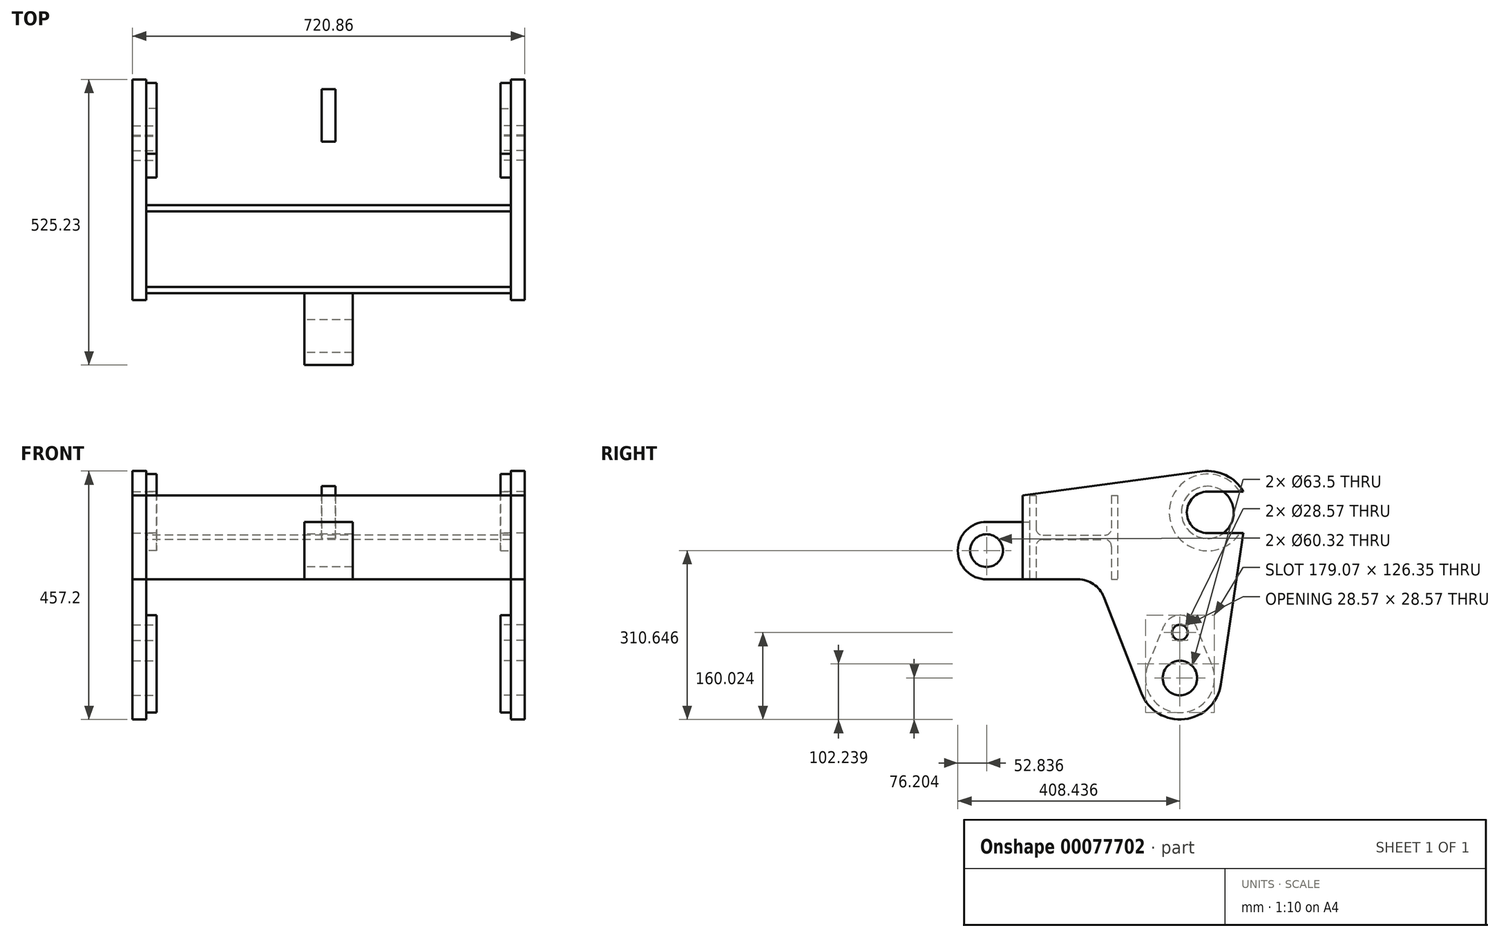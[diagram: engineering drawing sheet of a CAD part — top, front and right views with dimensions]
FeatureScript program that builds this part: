
annotation { "Feature Type Name" : "Feature", "Feature Type Description" : "" }
export const myFeature = defineFeature(function(context is Context, id is Id, definition is map)
    precondition{}
    {
        {
            var Q0;
            Q0=qCreatedBy(makeId("Right.planeOp"),FACE);
            var sketch = newSketch(context, id + "F0", { "sketchPlane" : qUnion([Q0])});
            skLineSegment(sketch, "E0.rect.bottom", {"start": v(-81.03, 77.22) * mm, "end": v(-69.47, 77.22) * mm});
            skLineSegment(sketch, "E0.rect.top", {"start": v(-81.03, -77.22) * mm, "end": v(-69.47, -77.22) * mm});
            skLineSegment(sketch, "E0.rect.left", {"start": v(-81.03, 77.22) * mm, "end": v(-81.03, -77.22) * mm});
            skLineSegment(sketch, "E0.rect.right", {"start": v(81.03, 77.22) * mm, "end": v(81.03, -77.22) * mm});
            skPoint(sketch, "E0.rect.middle", {"position": v(0, 0) * mm});
            skLineSegment(sketch, "E1.0", {"start": v(-69.47, 77.22) * mm, "end": v(-69.47, -77.22) * mm});
            skLineSegment(sketch, "E2", {"start": v(-81.03, 0) * mm, "end": v(81.03, 0) * mm, "construction": true});
            skLineSegment(sketch, "E3", {"start": v(0, 77.22) * mm, "end": v(0, -77.22) * mm, "construction": true});
            skLineSegment(sketch, "E4.0", {"start": v(-81.03, -4.06) * mm, "end": v(81.03, -4.06) * mm});
            skLineSegment(sketch, "E5.0.MirrorCS", {"start": v(-81.03, 4.06) * mm, "end": v(81.03, 4.06) * mm});
            skLineSegment(sketch, "E6.0.MirrorCS", {"start": v(69.47, 77.22) * mm, "end": v(69.47, -77.22) * mm});
            skLineSegment(sketch, "E7.trimOffspring", {"start": v(69.47, 77.22) * mm, "end": v(81.03, 77.22) * mm});
            skLineSegment(sketch, "E8.trimOffspring", {"start": v(69.47, -77.22) * mm, "end": v(81.03, -77.22) * mm});
            skSolve(sketch);
        }
        {
            var Q0;
            Q0=qSketchRegion(id+"F0",true);
            extrude(context, id + "F1", {"entities" : qUnion([Q0]), "endBound" : BoundingType.SYMMETRIC, "depth" : 670.05 * mm});
        }
        {
            var Q0;
            Q0=makeQuery(id+"F1.opExtrude","SWEPT_EDGE",EDGE,{"disambiguationData":[OSD([sQuery(id+"F0.wireOp",EDGE,"E5.0.MirrorCS"),sQuery(id+"F0.wireOp",EDGE,"E6.0.MirrorCS")])]});
            var Q1;
            Q1=makeQuery(id+"F1.opExtrude","SWEPT_EDGE",EDGE,{"disambiguationData":[OSD([sQuery(id+"F0.wireOp",EDGE,"E4.0"),sQuery(id+"F0.wireOp",EDGE,"E6.0.MirrorCS")])]});
            var Q2;
            Q2=makeQuery(id+"F1.opExtrude","SWEPT_EDGE",EDGE,{"disambiguationData":[OSD([sQuery(id+"F0.wireOp",EDGE,"E1.0"),sQuery(id+"F0.wireOp",EDGE,"E5.0.MirrorCS")])]});
            var Q3;
            Q3=makeQuery(id+"F1.opExtrude","SWEPT_EDGE",EDGE,{"disambiguationData":[OSD([sQuery(id+"F0.wireOp",EDGE,"E1.0"),sQuery(id+"F0.wireOp",EDGE,"E4.0")])]});
            fillet(context, id + "F2", {"entities" : qUnion([Q0, Q1, Q2, Q3]), "radius" : 12.7 * mm, "tangentPropagation" : true, "allowEdgeOverflow" : false});
        }
        {
            var Q0;
            Q0=makeQuery(id+"F1.opExtrude","CAP_FACE",FACE,{"disambiguationData":[OSD([sQuery(id+"F0.wireOp",EDGE,"E0.rect.bottom"),sQuery(id+"F0.wireOp",EDGE,"E0.rect.top"),sQuery(id+"F0.wireOp",EDGE,"E0.rect.left"),sQuery(id+"F0.wireOp",EDGE,"E0.rect.right"),sQuery(id+"F0.wireOp",EDGE,"E1.0"),sQuery(id+"F0.wireOp",EDGE,"E4.0"),sQuery(id+"F0.wireOp",EDGE,"E5.0.MirrorCS"),sQuery(id+"F0.wireOp",EDGE,"E6.0.MirrorCS"),sQuery(id+"F0.wireOp",EDGE,"E7.trimOffspring"),sQuery(id+"F0.wireOp",EDGE,"E8.trimOffspring")])],"isStart":false});
            var sketch = newSketch(context, id + "F3", { "sketchPlane" : qUnion([Q0])});
            skLineSegment(sketch, "E9", {"start": v(-81.03, -4.06) * mm, "end": v(-81.03, 203.68) * mm, "construction": true});
            skLineSegment(sketch, "E10.0", {"start": v(246.13, -4.06) * mm, "end": v(246.13, 203.68) * mm, "construction": true});
            skLineSegment(sketch, "E11", {"start": v(81.03, 0) * mm, "end": v(356.17, 0) * mm, "construction": true});
            skLineSegment(sketch, "E12.0", {"start": v(81.03, 45.97) * mm, "end": v(356.17, 45.97) * mm, "construction": true});
            skArc(sketch, "E13", {"start": v(312.12, 84.07) * mm, "mid": v(279.74, 114.36) * mm, "end": v(235.98, 121.5) * mm});
            skArc(sketch, "E14", {"start": v(246.13, 84.07) * mm, "mid": v(208.03, 45.97) * mm, "end": v(246.13, 7.87) * mm});
            skLineSegment(sketch, "E15", {"start": v(246.13, 84.07) * mm, "end": v(312.12, 84.07) * mm});
            skLineSegment(sketch, "E16", {"start": v(246.13, 7.87) * mm, "end": v(312.12, 7.87) * mm});
            skLineSegment(sketch, "E17.0", {"start": v(81.03, -258.83) * mm, "end": v(356.17, -258.83) * mm, "construction": true});
            skLineSegment(sketch, "E18.0", {"start": v(195.33, -258.83) * mm, "end": v(195.33, 203.68) * mm, "construction": true});
            skCircle(sketch, "E19", {"center": v(195.33, -258.83) * mm, "radius": 31.75 * mm});
            skArc(sketch, "E20", {"start": v(124.35, -286.55) * mm, "mid": v(209.43, -333.7) * mm, "end": v(271.53, -258.83) * mm});
            skLineSegment(sketch, "E21.0", {"start": v(-93.73, 77.22) * mm, "end": v(-93.73, -77.22) * mm});
            skLineSegment(sketch, "E22", {"start": v(-93.73, 77.22) * mm, "end": v(235.98, 121.5) * mm});
            skLineSegment(sketch, "E23.0", {"start": v(7.87, 77.22) * mm, "end": v(7.87, -128.02) * mm, "construction": true});
            skLineSegment(sketch, "E24", {"start": v(-93.73, -77.22) * mm, "end": v(7.87, -77.22) * mm});
            skLineSegment(sketch, "E25.0", {"start": v(-93.73, -128.02) * mm, "end": v(133.5, -128.02) * mm, "construction": true});
            skArc(sketch, "E26", {"start": v(55.2, -109.53) * mm, "mid": v(36.52, -86.07) * mm, "end": v(7.87, -77.22) * mm});
            skLineSegment(sketch, "E27.trimOffspring", {"start": v(113.52, -258.83) * mm, "end": v(124.35, -286.55) * mm});
            skLineSegment(sketch, "E28", {"start": v(113.52, -258.83) * mm, "end": v(55.2, -109.53) * mm});
            skLineSegment(sketch, "E29", {"start": v(312.12, 7.87) * mm, "end": v(270.7, -270.06) * mm});
            skSolve(sketch);
        }
        {
            var Q0;
            Q0=qSketchRegion(id+"F3",true);
            extrude(context, id + "F4", {"entities" : qUnion([Q0]), "operationType" : NewBodyOperationType.ADD, "depth" : 25.4 * mm});
        }
        {
            var Q0;
            Q0=makeQuery(id+"F4.opExtrude","CAP_FACE",FACE,{"disambiguationData":[OSD([sQuery(id+"F3.wireOp",EDGE,"E13"),sQuery(id+"F3.wireOp",EDGE,"E14"),sQuery(id+"F3.wireOp",EDGE,"E15"),sQuery(id+"F3.wireOp",EDGE,"E16"),sQuery(id+"F3.wireOp",EDGE,"E19"),sQuery(id+"F3.wireOp",EDGE,"E20"),sQuery(id+"F3.wireOp",EDGE,"E21.0"),sQuery(id+"F3.wireOp",EDGE,"E22"),sQuery(id+"F3.wireOp",EDGE,"E24"),sQuery(id+"F3.wireOp",EDGE,"E26"),sQuery(id+"F3.wireOp",EDGE,"E27.trimOffspring"),sQuery(id+"F3.wireOp",EDGE,"E28"),sQuery(id+"F3.wireOp",EDGE,"E29")])],"isStart":true});
            var sketch = newSketch(context, id + "F5", { "sketchPlane" : qUnion([Q0])});
            skArc(sketch, "E30", {"start": v(-254.1, -234.77) * mm, "mid": v(-195.33, -322.33) * mm, "end": v(-136.56, -234.77) * mm});
            skLineSegment(sketch, "E31", {"start": v(-195.33, -258.83) * mm, "end": v(-195.33, -175) * mm, "construction": true});
            skArc(sketch, "E32", {"start": v(-165.94, -162.98) * mm, "mid": v(-195.33, -143.26) * mm, "end": v(-224.71, -162.98) * mm});
            skCircle(sketch, "E33.0", {"center": v(-195.33, -258.83) * mm, "radius": 31.75 * mm});
            skLineSegment(sketch, "E34", {"start": v(-254.1, -234.77) * mm, "end": v(-224.71, -162.98) * mm});
            skLineSegment(sketch, "E35.0.MirrorCS", {"start": v(-136.56, -234.77) * mm, "end": v(-165.94, -162.98) * mm});
            skSolve(sketch);
        }
        {
            var Q0;
            Q0=qSketchRegion(id+"F5",true);
            extrude(context, id + "F6", {"entities" : qUnion([Q0]), "operationType" : NewBodyOperationType.ADD, "depth" : 19.05 * mm});
        }
        {
            var Q0;
            Q0=makeQuery(id+"F6.opExtrude","CAP_FACE",FACE,{"disambiguationData":[OSD([sQuery(id+"F5.wireOp",EDGE,"E30"),sQuery(id+"F5.wireOp",EDGE,"E32"),sQuery(id+"F5.wireOp",EDGE,"E33.0"),sQuery(id+"F5.wireOp",EDGE,"E34"),sQuery(id+"F5.wireOp",EDGE,"E35.0.MirrorCS")])],"isStart":false});
            var sketch = newSketch(context, id + "F7", { "sketchPlane" : qUnion([Q0])});
            skCircle(sketch, "E36", {"center": v(-195.33, -175) * mm, "radius": 14.29 * mm});
            skSolve(sketch);
        }
        {
            var Q0;
            Q0=qSketchRegion(id+"F7",true);
            extrude(context, id + "F8", {"entities" : qUnion([Q0]), "operationType" : NewBodyOperationType.REMOVE, "endBound" : BoundingType.THROUGH_ALL, "oppositeDirection" : true, "depth" : 25.4 * mm});
        }
        {
            var Q0;
            Q0=makeQuery(id+"F4.opExtrude","CAP_FACE",FACE,{"disambiguationData":[OSD([sQuery(id+"F3.wireOp",EDGE,"E13"),sQuery(id+"F3.wireOp",EDGE,"E14"),sQuery(id+"F3.wireOp",EDGE,"E15"),sQuery(id+"F3.wireOp",EDGE,"E16"),sQuery(id+"F3.wireOp",EDGE,"E19"),sQuery(id+"F3.wireOp",EDGE,"E20"),sQuery(id+"F3.wireOp",EDGE,"E21.0"),sQuery(id+"F3.wireOp",EDGE,"E22"),sQuery(id+"F3.wireOp",EDGE,"E24"),sQuery(id+"F3.wireOp",EDGE,"E26"),sQuery(id+"F3.wireOp",EDGE,"E27.trimOffspring"),sQuery(id+"F3.wireOp",EDGE,"E28"),sQuery(id+"F3.wireOp",EDGE,"E29")])],"isStart":true});
            var sketch = newSketch(context, id + "F9", { "sketchPlane" : qUnion([Q0])});
            skArc(sketch, "E37", {"start": v(-305.64, 7.87) * mm, "mid": v(-175.46, 45.97) * mm, "end": v(-305.64, 84.07) * mm});
            skLineSegment(sketch, "E38.0", {"start": v(-246.13, 84.07) * mm, "end": v(-312.12, 84.07) * mm});
            skArc(sketch, "E39.0", {"start": v(-246.13, 84.07) * mm, "mid": v(-208.03, 45.97) * mm, "end": v(-246.13, 7.87) * mm});
            skLineSegment(sketch, "E40.0", {"start": v(-246.13, 7.87) * mm, "end": v(-312.12, 7.87) * mm});
            skSolve(sketch);
        }
        {
            var Q0;
            Q0=qSketchRegion(id+"F9",true);
            extrude(context, id + "F10", {"entities" : qUnion([Q0]), "operationType" : NewBodyOperationType.ADD, "depth" : 19.05 * mm});
        }
        {
            var Q0;
            Q0=qCreatedBy(makeId("Right.planeOp"),FACE);
            var sketch = newSketch(context, id + "F11", { "sketchPlane" : qUnion([Q0])});
            skLineSegment(sketch, "E41.0", {"start": v(-160.27, 77.22) * mm, "end": v(-160.27, -77.22) * mm, "construction": true});
            skLineSegment(sketch, "E42.0", {"start": v(-81.03, 77.22) * mm, "end": v(-81.03, -77.22) * mm, "construction": true});
            skLineSegment(sketch, "E43", {"start": v(-81.03, 77.22) * mm, "end": v(-252.94, 77.22) * mm, "construction": true});
            skLineSegment(sketch, "E44.0", {"start": v(-81.03, -24.38) * mm, "end": v(-252.94, -24.38) * mm, "construction": true});
            skArc(sketch, "E45", {"start": v(-160.27, 28.45) * mm, "mid": v(-213.1, -24.38) * mm, "end": v(-160.27, -77.22) * mm});
            skCircle(sketch, "E46", {"center": v(-160.27, -24.38) * mm, "radius": 30.16 * mm});
            skLineSegment(sketch, "E47", {"start": v(-160.27, 28.45) * mm, "end": v(-81.03, 28.45) * mm});
            skLineSegment(sketch, "E48", {"start": v(-81.03, 28.45) * mm, "end": v(-81.03, -77.22) * mm});
            skLineSegment(sketch, "E49", {"start": v(-160.27, -77.22) * mm, "end": v(-81.03, -77.22) * mm});
            skSolve(sketch);
        }
        {
            var Q0;
            Q0=qSketchRegion(id+"F11",true);
            extrude(context, id + "F12", {"entities" : qUnion([Q0]), "operationType" : NewBodyOperationType.ADD, "endBound" : BoundingType.SYMMETRIC, "depth" : 88.9 * mm});
        }
        {
            var Q0;
            Q0=makeQuery(id+"F1.opExtrude","SWEPT_BODY",BODY,{"disambiguationData":[OSD([sQuery(id+"F0.wireOp",EDGE,"E0.rect.bottom"),sQuery(id+"F0.wireOp",EDGE,"E0.rect.top"),sQuery(id+"F0.wireOp",EDGE,"E0.rect.left"),sQuery(id+"F0.wireOp",EDGE,"E0.rect.right"),sQuery(id+"F0.wireOp",EDGE,"E1.0"),sQuery(id+"F0.wireOp",EDGE,"E4.0"),sQuery(id+"F0.wireOp",EDGE,"E5.0.MirrorCS"),sQuery(id+"F0.wireOp",EDGE,"E6.0.MirrorCS"),sQuery(id+"F0.wireOp",EDGE,"E7.trimOffspring"),sQuery(id+"F0.wireOp",EDGE,"E8.trimOffspring")])]});
            var Q1;
            Q1=qCreatedBy(makeId("Right.planeOp"),FACE);
            mirror(context, id + "F13", {"entities" : qUnion([Q0]), "mirrorPlane" : qUnion([Q1])});
        }
        {
            var Q0;
            Q0=qCreatedBy(makeId("Right.planeOp"),FACE);
            var sketch = newSketch(context, id + "F14", { "sketchPlane" : qUnion([Q0])});
            skArc(sketch, "E50.0", {"start": v(246.13, 84.07) * mm, "mid": v(208.03, 45.97) * mm, "end": v(246.13, 7.87) * mm, "construction": true});
            skCircle(sketch, "E51", {"center": v(246.13, 45.97) * mm, "radius": 48.05 * mm});
            skSolve(sketch);
        }
        {
            var Q0;
            Q0=qSketchRegion(id+"F14",true);
            extrude(context, id + "F15", {"entities" : qUnion([Q0]), "endBound" : BoundingType.SYMMETRIC, "depth" : 25.4 * mm});
        }
    });
